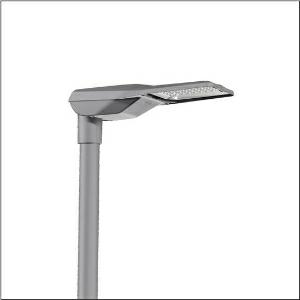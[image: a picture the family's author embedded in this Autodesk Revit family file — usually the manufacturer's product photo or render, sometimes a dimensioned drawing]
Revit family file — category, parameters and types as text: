
# Revit family: streetlight_sl_21_iq_mini___st1_5a_5xe2p41d08hb_72ee
name_source: partatom
category: Lighting Fixtures
units: mm (PartAtom-declared; Revit-internal decimal feet)

## family parameters
Cut with Voids When Loaded = No
Host = Face
Light Source = No
Part Type = Normal
Room Calculation Point = No
Round Connector Dimension = Use Diameter
Shared = No

## types (1)
- --- (1 x LED, 9690 lm, 70.9 W, 4000K)
    Apparent Load = 71 VA
    CIE Flux Codes = 22 53 95 100 100
    Color Rendering = 70
    Color Temperature = 4000K
    Default Elevation = 1800 mm
    Description = Streetlight SL 21 iQ mini, mast luminaire, primary light control with lens, of PMMA, primary optical cover: cover, of toughened safety glass, transparent, light distribution: ST1.5a, light emission: direct distribution, primary light characteristic: asymmetric, installation type: post-top, side-entry, LED, High Power LED, rated luminous flux: 9.690lm, luminous efficacy: 137lm/W, light colour: 740, colour temperature: 4000K, control gear: iQ-Comfort, control: Auto-Match, Temp-Guard, Lumen-Switch, Night-Set, Smart-Wire, Light-Fading, Desk-Remote (wireless, voltage-free reading and setting of iQ features in the workshop via application-optimized NFC function/RFID function), optimised constant luminous flux control (CLO 2.0), pre-setting: linear dimming characteristic, mains connection: 220..240V, AC, 50/60Hz, start of lifetime: 71W, end of service life: 75W, reduction: 31W, luminaire housing, of diecast aluminium, powder-coated, SITECO metallic grey (DB 702S), corrosivity category C5 high according to DIN EN ISO 12944, please order mast flange separately, inclination adjustable: 0°, 5°, 10°, 15°, sealing non-destructively replaceable, multi-level sealing system, length: 628mm, width: 235mm, height: 110mm, mast flange for spigot size: 42mm (side-entry): 5XC10008XM4, 60/48mm (side-entry/post-top): 5XC10108XM2, 76/60mm (side-entry/post-top): 5XC10108XM1, mounting height: 4..8m, protection rating (complete): IP66, insulation class (complete): insulation class II (safety insulation), certification: CE, ENEC, ENEC+, VDE, impact resistance: IK10, permissible operating ambient temperature for outdoor applications: -40..+50°C, standard-compliant lighting for roads and squares, packaging unit: 1 piece

Light Distribution: ST1.5a
    Height = 110 mm
    Lamp = 1 x LED
    Lamp Light Flux = 9690 lm
    Lamp Power = 70.9 W
    Lamp count = 1
    Length = 625 mm
    Luminous efficacy = 137 lm/W
    Manufacturer = Siteco
    ModVariant = No
    Model = 5XE2P41D08HB
    Number of Poles = 1
    OnlyDefault = Yes
    Power Factor = 1
    Product Name = Streetlight SL 21 iQ mini | ST1.5a
    Product group = mast luminaire | pylon top
    ProductGroupID = 6100
    Protection Class = Protection class II
    Protection Degree = IP 66
    RLX_Detail_Level = 1
    RLX_Emergency_Light_Flux = 0 lm
    RLX_Emergency_Type = 0
    RLX_Emergency_Type_DB = No
    RlxData = <blob elided: 29861 chars, md5=df17ca05>
    Socket = socket
    Standby Power = 0 W
    System Light Flux = 9690 lm
    System Power = 71 W
    Type Comments = factory setting: luminous flux: 100 % | dim-lin: 254 | 711 mA
    Type Image = l_1003519.jpg
    URL = http://relux.com
    VarID = @adj_156501
    Voltage = 0 V
    Weight = 0.00 kg
    Width = 234 mm

## geometry (parser evidence)
native form markers: Blend x4, Sweep x9
no freeform markers — native parametric forms only
